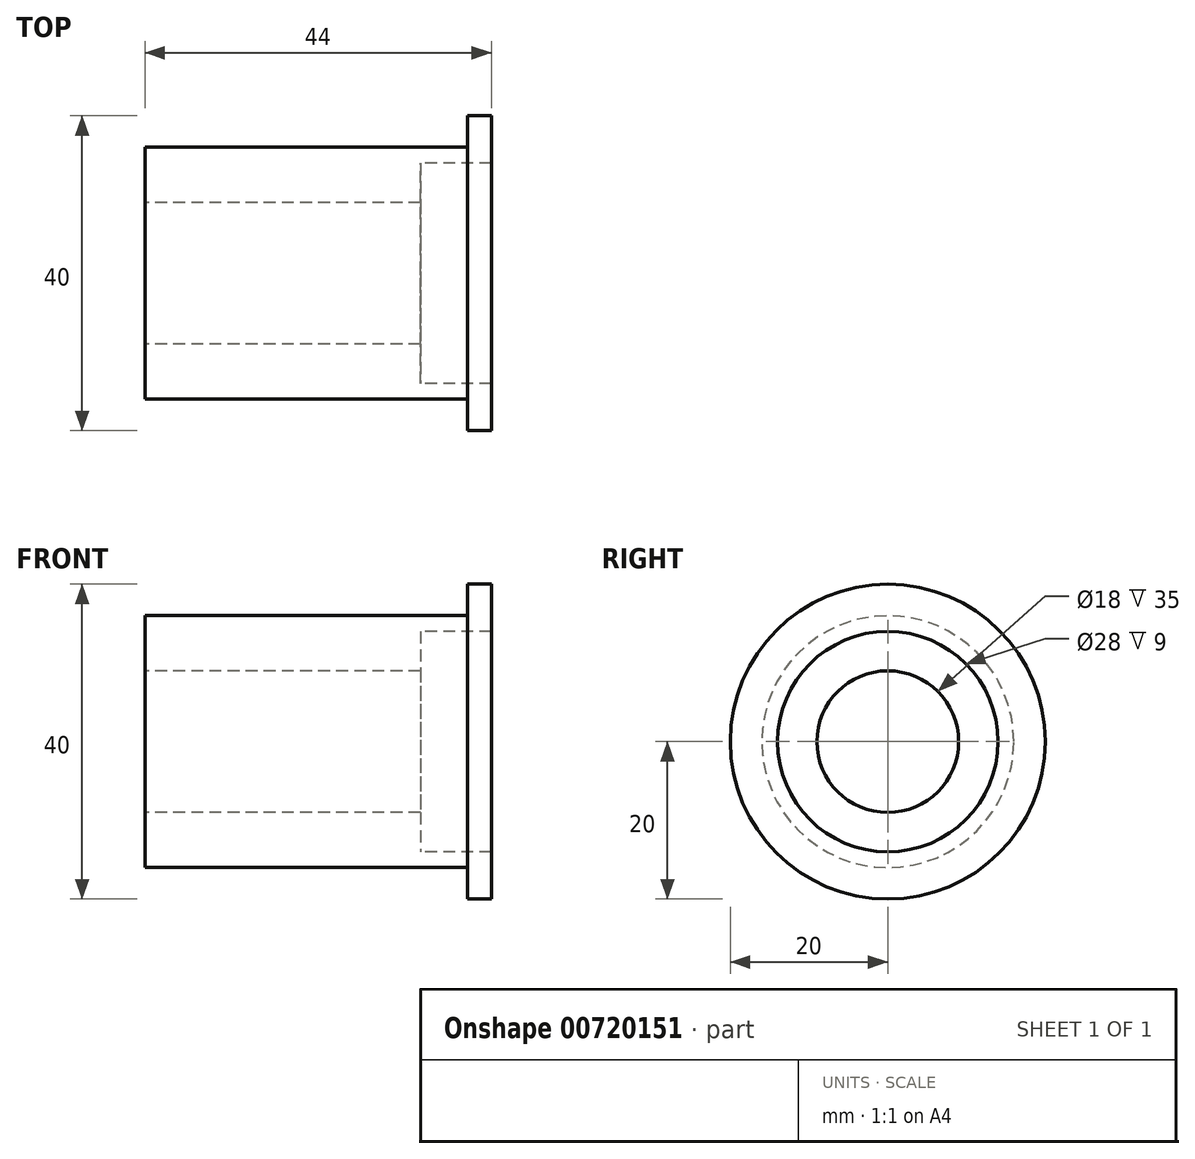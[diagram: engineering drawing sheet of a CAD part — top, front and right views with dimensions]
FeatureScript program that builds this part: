
annotation { "Feature Type Name" : "Feature", "Feature Type Description" : "" }
export const myFeature = defineFeature(function(context is Context, id is Id, definition is map)
    precondition{}
    {
        {
            var Q0;
            Q0=qCreatedBy(makeId("Front.planeOp"),FACE);
            var sketch = newSketch(context, id + "F0", { "sketchPlane" : qUnion([Q0])});
            skLineSegment(sketch, "E0", {"start": v(0, 9) * mm, "end": v(0, 16) * mm});
            skLineSegment(sketch, "E1", {"start": v(0, 16) * mm, "end": v(41, 16) * mm});
            skLineSegment(sketch, "E2", {"start": v(41, 16) * mm, "end": v(41, 20) * mm});
            skLineSegment(sketch, "E3", {"start": v(41, 20) * mm, "end": v(44, 20) * mm});
            skLineSegment(sketch, "E4", {"start": v(44, 20) * mm, "end": v(44, 14) * mm});
            skLineSegment(sketch, "E5", {"start": v(44, 14) * mm, "end": v(35, 14) * mm});
            skLineSegment(sketch, "E6", {"start": v(35, 14) * mm, "end": v(35, 9) * mm});
            skLineSegment(sketch, "E7", {"start": v(35, 9) * mm, "end": v(0, 9) * mm});
            skLineSegment(sketch, "E8", {"start": v(0, 0) * mm, "end": v(9.3, 0) * mm});
            skSolve(sketch);
        }
        {
            var Q0;
            Q0=makeQuery(id+"F0.imprint","IMPRINT",FACE,{"disambiguationData":[TD([[makeQuery(id+"F0.imprint","IMPRINT",EDGE,{"derivedFrom":sQuery(id+"F0.wireOp",EDGE,"E0")}),-1.0]])]});
            var Q1;
            Q1=sQuery(id+"F0.wireOp",EDGE,"E8");
            revolve(context, id + "F1", {"surfaceOperationType" : NewSurfaceOperationType.NEW, "entities" : qUnion([Q0]), "axis" : qUnion([Q1]), "revolveType" : RevolveType.FULL});
        }
    });
